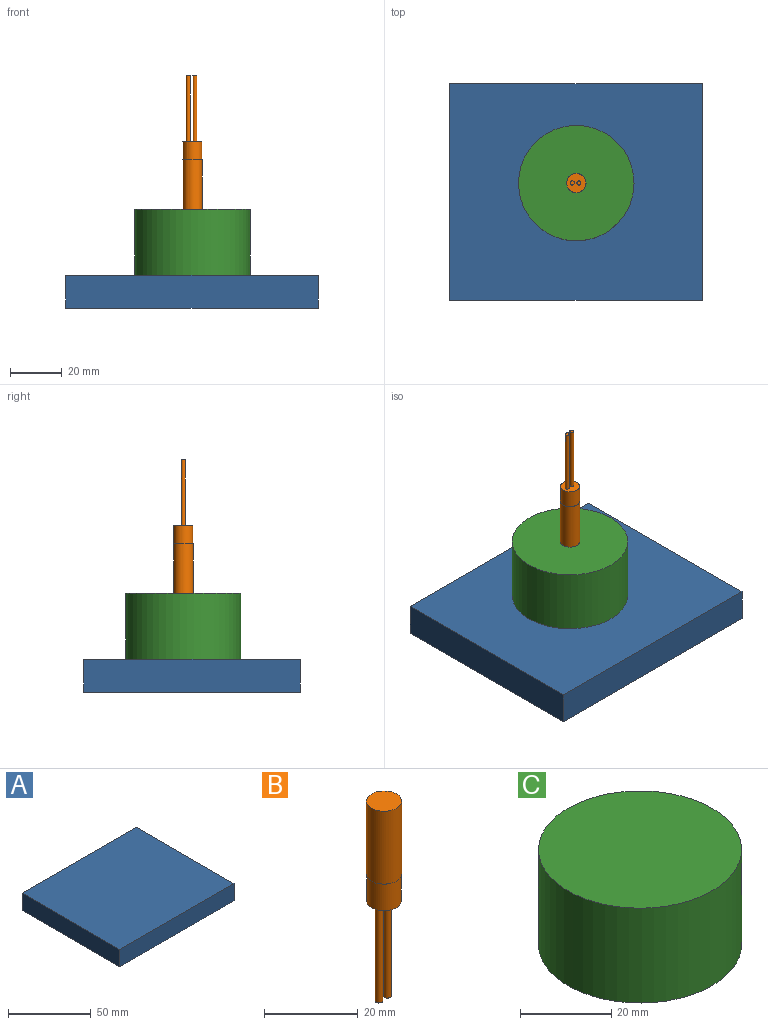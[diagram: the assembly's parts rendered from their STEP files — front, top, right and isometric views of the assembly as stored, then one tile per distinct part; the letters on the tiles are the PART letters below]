
ASSEMBLY  parts=3 mates=3
PART A: 6 faces, bbox 97.3x83.5x12.7 mm
  f0: plane 97.28x12.7mm, normal (0,1,0), area 1235.4mm2, adj f1,f3,f4,f5
  f1: plane 83.49x12.7mm, normal (-1,0,0), area 1060.3mm2, adj f0,f2,f4,f5
  f2: plane 97.28x12.7mm, normal (0,-1,0), area 1235.4mm2, adj f1,f3,f4,f5
  f3: plane 83.49x12.7mm, normal (1,0,0), area 1060.3mm2, adj f0,f2,f4,f5
  f4: plane 97.28x83.49mm, normal (0,0,1), area 8121.8mm2, adj f0,f1,f2,f3
  f5: plane 97.28x83.49mm, normal (0,0,-1), area 8121.8mm2, adj f0,f1,f2,f3
PART B: 9 faces, bbox 7.5x7.5x51.4 mm
  f0: cylinder r=3.68mm len=7.37mm, axis (0,0,1), area 161.6mm2, adj f1,f8
  f1: plane 7.37x7.37mm, normal (0,0,-1), area 38.7mm2, adj f0,f2,f4
  f2: cylinder r=0.79mm len=25.4mm, axis (0,0,1), area 125.7mm2, adj f1,f3
  f3: plane 1.57x1.57mm, normal (0,0,-1), area 1.9mm2, adj f2
  f4: cylinder r=0.79mm len=25.4mm, axis (0,0,1), area 125.7mm2, adj f1,f5
  f5: plane 1.57x1.57mm, normal (0,0,-1), area 1.9mm2, adj f4
  f6: cylinder r=3.75mm len=19.05mm, axis (0,0,-1), area 448.4mm2, adj f7,f8
  f7: plane 7.49x7.49mm, normal (0,0,1), area 44.1mm2, adj f6
  f8: plane 7.49x7.49mm, normal (0,0,-1), area 1.5mm2, adj f0,f6
PART C: 3 faces, bbox 44.5x44.5x25.4 mm
  f0: cylinder r=22.23mm len=44.45mm, axis (0,0,-1), area 3547mm2, adj f1,f2
  f1: plane 44.45x44.45mm, normal (0,0,1), area 1551.8mm2, adj f0
  f2: plane 44.45x44.45mm, normal (0,0,-1), area 1551.8mm2, adj f0
PLACE A t=(-27.26,3.06,-9.77)mm fixed
PLACE B rot(axis=(1,0,0),180deg) t=(-25.19,-13.53,47.38)mm
PLACE C t=(-25.19,-13.53,2.93)mm
MATE planar C.f0 <-> A.f4  axis (0,0,-1) through (-25.19,-13.53,2.93)mm
MATE cylindrical B.f0 <-> C.f0  axis (0,0,1) through (-25.19,-13.53,37.85)mm
MATE planar B.f0 <-> C.f0  axis (0,0,-1) through (-25.19,-13.53,28.33)mm
